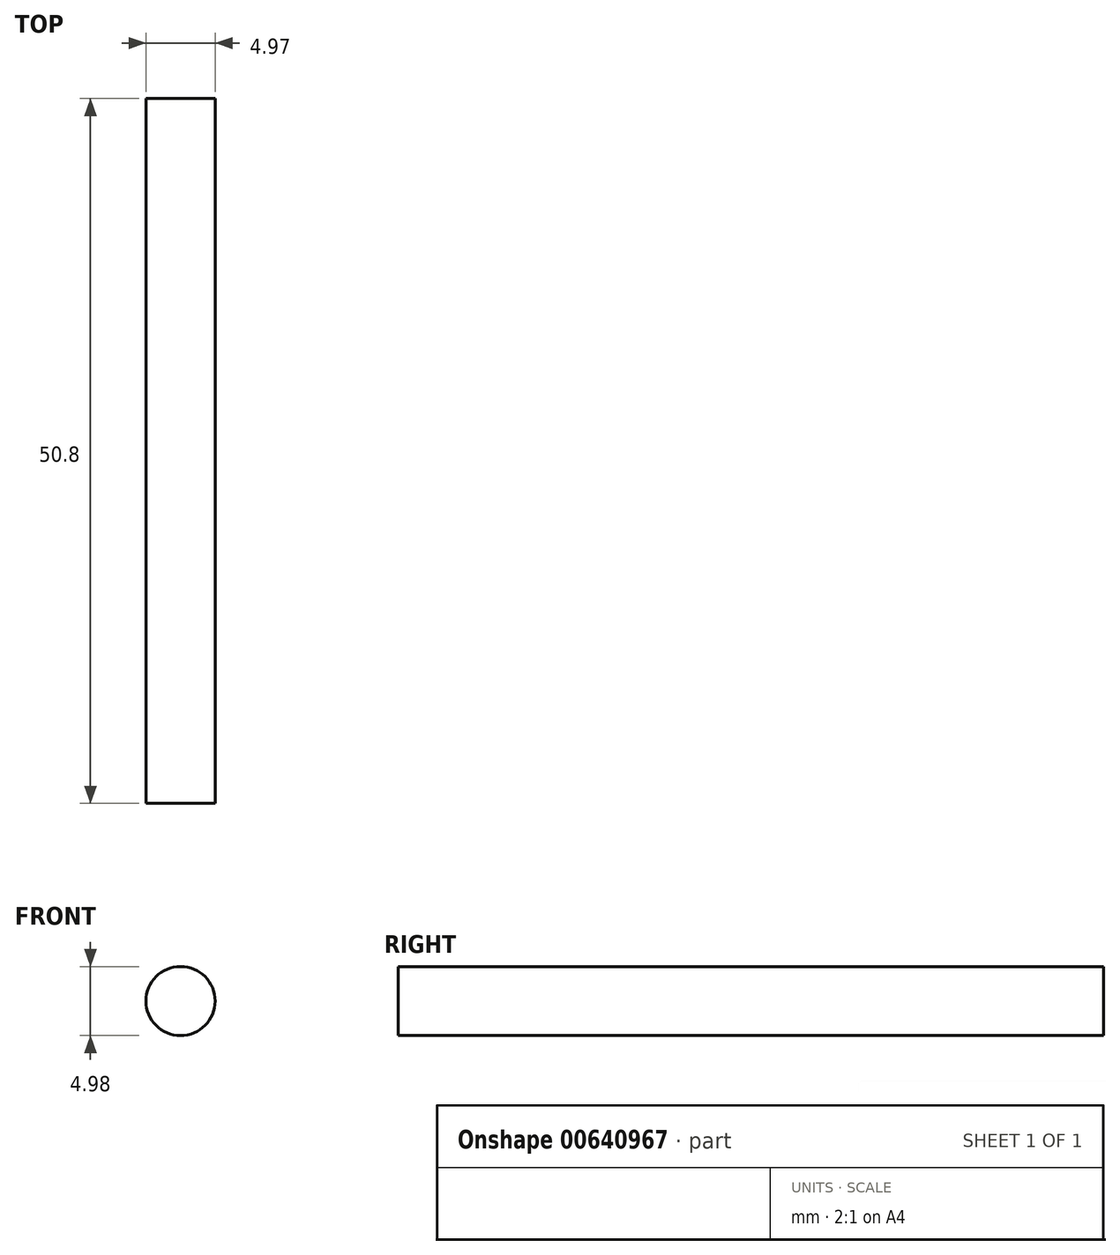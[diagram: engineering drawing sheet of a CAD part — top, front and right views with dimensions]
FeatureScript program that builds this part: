
annotation { "Feature Type Name" : "Feature", "Feature Type Description" : "" }
export const myFeature = defineFeature(function(context is Context, id is Id, definition is map)
    precondition{}
    {
        {
            var Q0;
            Q0=qCreatedBy(makeId("Front.planeOp"),FACE);
            var sketch = newSketch(context, id + "F0", { "sketchPlane" : qUnion([Q0])});
            skCircle(sketch, "E0", {"center": v(-23.47, 34.63) * mm, "radius": 2.49 * mm});
            skSolve(sketch);
        }
        {
            var Q0;
            Q0=makeQuery(id+"F0.imprint","IMPRINT",FACE,{"disambiguationData":[TD([[makeQuery(id+"F0.imprint","IMPRINT",EDGE,{"derivedFrom":sQuery(id+"F0.wireOp",EDGE,"E0")}),1.0]])]});
            extrude(context, id + "F1", {"entities" : qUnion([Q0]), "depth" : 50.8 * mm, "offsetDistance" : 25.4 * mm});
        }
    });
